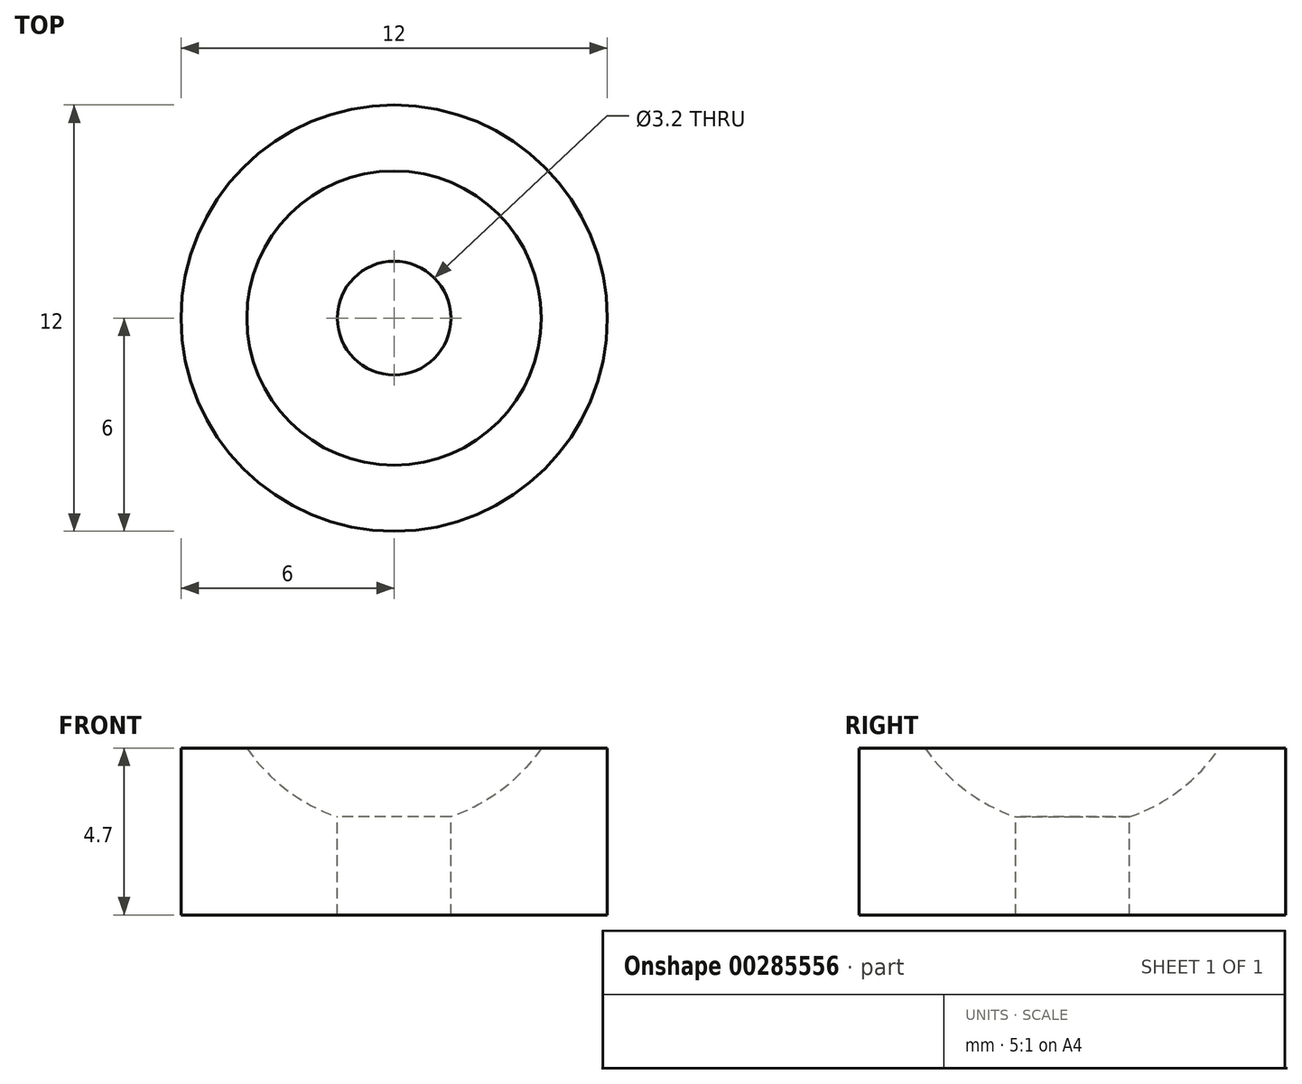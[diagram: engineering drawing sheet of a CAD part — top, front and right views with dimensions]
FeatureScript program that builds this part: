
annotation { "Feature Type Name" : "Feature", "Feature Type Description" : "" }
export const myFeature = defineFeature(function(context is Context, id is Id, definition is map)
    precondition{}
    {
        {
            var Q0;
            Q0=qCreatedBy(makeId("Top.planeOp"),FACE);
            var sketch = newSketch(context, id + "F0", { "sketchPlane" : qUnion([Q0])});
            skCircle(sketch, "E0", {"center": v(0, 0) * mm, "radius": 6 * mm});
            skSolve(sketch);
        }
        {
            var Q0;
            Q0=makeQuery(id+"F0.imprint","IMPRINT",FACE,{"disambiguationData":[TD([[makeQuery(id+"F0.imprint","IMPRINT",EDGE,{"derivedFrom":sQuery(id+"F0.wireOp",EDGE,"E0")}),1.0]])]});
            extrude(context, id + "F1", {"entities" : qUnion([Q0]), "depth" : 4.7 * mm});
        }
        {
            var Q0;
            Q0=makeQuery(id+"F1.opExtrude","CAP_FACE",FACE,{"disambiguationData":[OSD([sQuery(id+"F0.wireOp",EDGE,"E0")])],"isStart":false});
            var sketch = newSketch(context, id + "F2", { "sketchPlane" : qUnion([Q0])});
            skCircle(sketch, "E1", {"center": v(0, 0) * mm, "radius": 1.6 * mm});
            skSolve(sketch);
        }
        {
            var Q0;
            Q0=makeQuery(id+"F2.imprint","IMPRINT",FACE,{"disambiguationData":[TD([[makeQuery(id+"F2.imprint","IMPRINT",EDGE,{"derivedFrom":sQuery(id+"F2.wireOp",EDGE,"E1")}),1.0]])]});
            extrude(context, id + "F3", {"entities" : qUnion([Q0]), "operationType" : NewBodyOperationType.REMOVE, "oppositeDirection" : true, "depth" : 25 * mm});
        }
        {
            var Q0;
            Q0=qCreatedBy(makeId("Front.planeOp"),FACE);
            var sketch = newSketch(context, id + "F4", { "sketchPlane" : qUnion([Q0])});
            skArc(sketch, "E2", {"start": v(0, 12.5) * mm, "mid": v(-5, 7.5) * mm, "end": v(0, 2.5) * mm});
            skLineSegment(sketch, "E3", {"start": v(0, 12.5) * mm, "end": v(0, 2.5) * mm});
            skSolve(sketch);
        }
        {
            var Q0;
            Q0=makeQuery(id+"F4.imprint","IMPRINT",FACE,{"disambiguationData":[TD([[makeQuery(id+"F4.imprint","IMPRINT",EDGE,{"derivedFrom":sQuery(id+"F4.wireOp",EDGE,"E2")}),1.0]])]});
            var Q1;
            Q1=sQuery(id+"F4.wireOp",EDGE,"E3");
            revolve(context, id + "F5", {"operationType" : NewBodyOperationType.REMOVE, "entities" : qUnion([Q0]), "axis" : qUnion([Q1]), "revolveType" : RevolveType.FULL, "oppositeDirection" : true});
        }
    });
